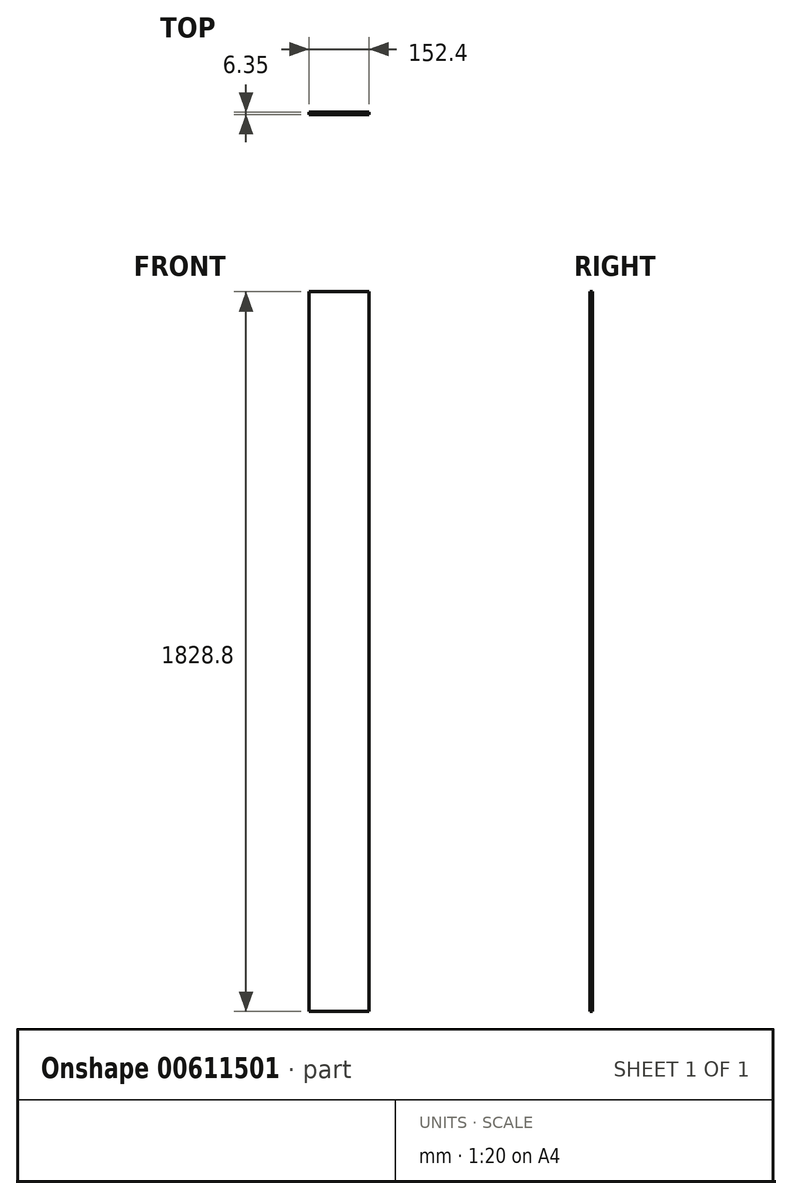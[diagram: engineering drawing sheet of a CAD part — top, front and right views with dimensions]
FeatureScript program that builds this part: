
annotation { "Feature Type Name" : "Feature", "Feature Type Description" : "" }
export const myFeature = defineFeature(function(context is Context, id is Id, definition is map)
    precondition{}
    {
        {
            var Q0;
            Q0=qCreatedBy(makeId("Front.planeOp"),FACE);
            var sketch = newSketch(context, id + "F0", { "sketchPlane" : qUnion([Q0])});
            skLineSegment(sketch, "E0.bottom", {"start": v(-424.44, 1081.75) * mm, "end": v(-272.04, 1081.75) * mm});
            skLineSegment(sketch, "E0.top", {"start": v(-424.44, -747.05) * mm, "end": v(-272.04, -747.05) * mm});
            skLineSegment(sketch, "E0.left", {"start": v(-424.44, 1081.75) * mm, "end": v(-424.44, -747.05) * mm});
            skLineSegment(sketch, "E0.right", {"start": v(-272.04, 1081.75) * mm, "end": v(-272.04, -747.05) * mm});
            skSolve(sketch);
        }
        {
            var Q0;
            Q0=makeQuery(id+"F0.imprint","IMPRINT",FACE,{"disambiguationData":[TD([[makeQuery(id+"F0.imprint","IMPRINT",EDGE,{"derivedFrom":sQuery(id+"F0.wireOp",EDGE,"E0.bottom")}),-1.0]])]});
            extrude(context, id + "F1", {"entities" : qUnion([Q0]), "depth" : 6.35 * mm, "offsetDistance" : 25.4 * mm});
        }
    });
